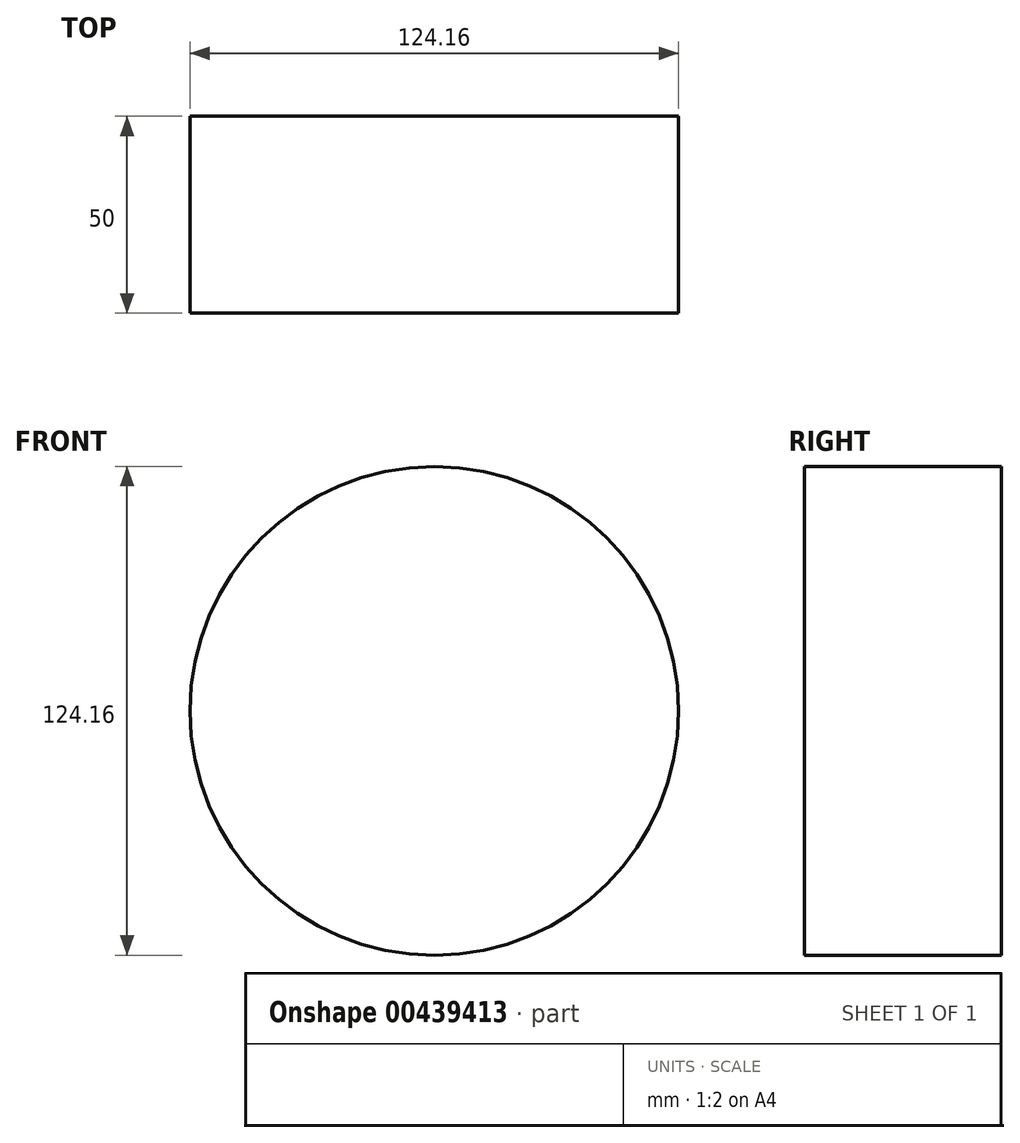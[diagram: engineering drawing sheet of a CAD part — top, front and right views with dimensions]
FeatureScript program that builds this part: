
annotation { "Feature Type Name" : "Feature", "Feature Type Description" : "" }
export const myFeature = defineFeature(function(context is Context, id is Id, definition is map)
    precondition{}
    {
        {
            var Q0;
            Q0=qCreatedBy(makeId("Front.planeOp"),FACE);
            var sketch = newSketch(context, id + "F0", { "sketchPlane" : qUnion([Q0])});
            skCircle(sketch, "E0", {"center": v(0, 0) * mm, "radius": 62.08 * mm});
            skSolve(sketch);
        }
        {
            var Q0;
            Q0 = qConstructionFilter(qBodyType(qCreatedBy(id + "F0" ,EDGE), BodyType.WIRE), ConstructionObject.NO);
            extrude(context, id + "F1", {"bodyType" : ToolBodyType.SURFACE, "surfaceEntities" : qUnion([Q0]), "depth" : 25 * mm, "hasSecondDirection" : true, "secondDirectionOppositeDirection" : true, "secondDirectionDepth" : 25 * mm});
        }
    });
